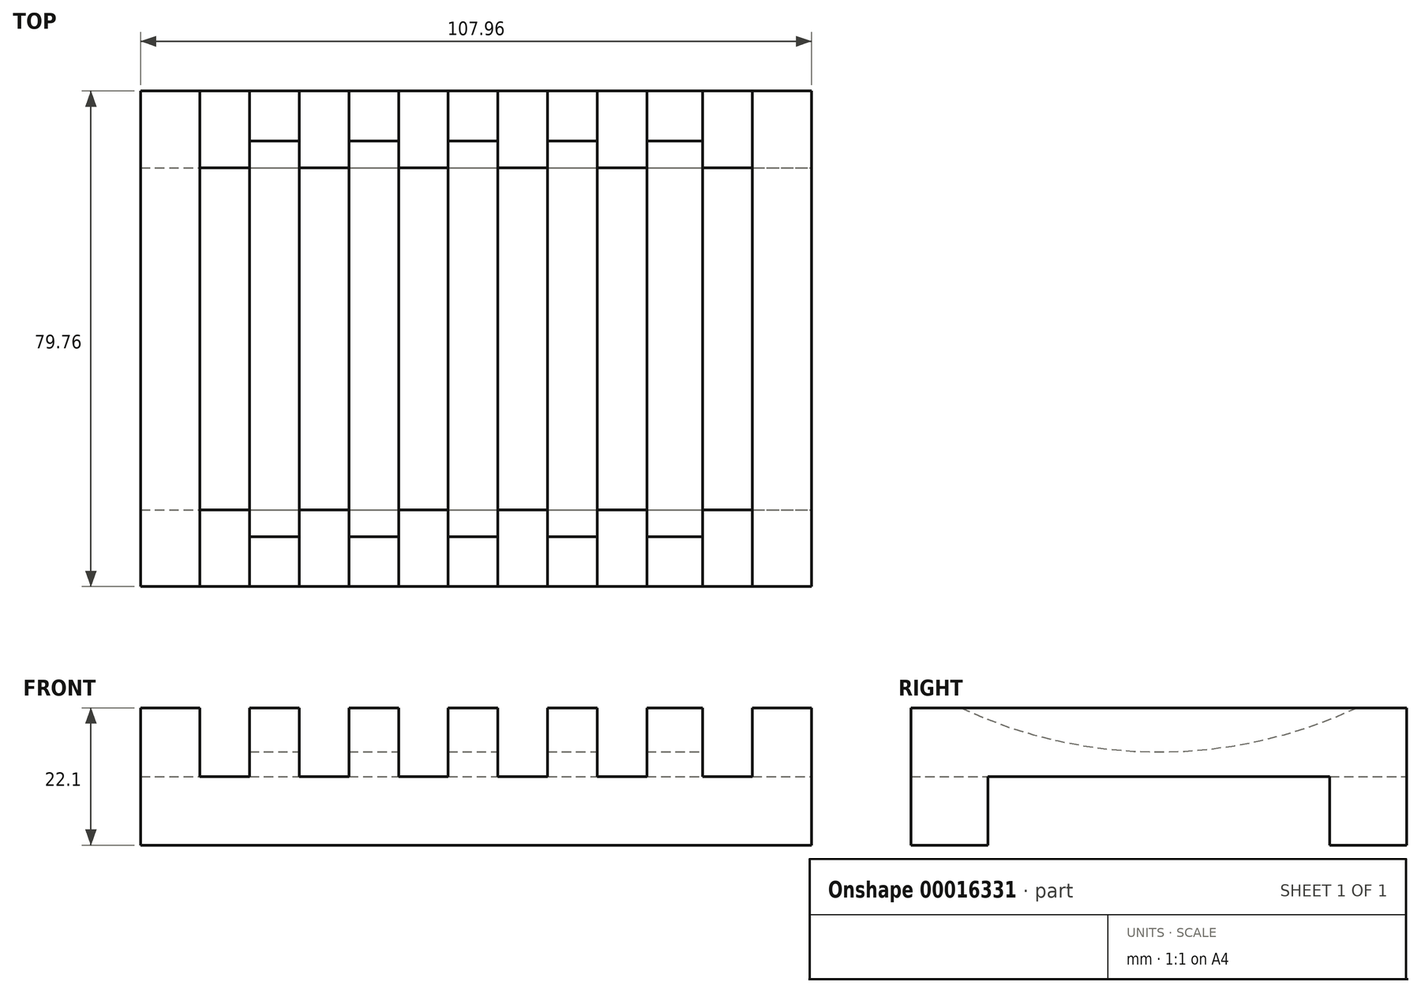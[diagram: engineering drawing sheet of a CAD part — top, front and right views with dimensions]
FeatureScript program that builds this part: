
annotation { "Feature Type Name" : "Feature", "Feature Type Description" : "" }
export const myFeature = defineFeature(function(context is Context, id is Id, definition is map)
    precondition{}
    {
        {
            var Q0;
            Q0=qCreatedBy(makeId("Top.planeOp"),FACE);
            var sketch = newSketch(context, id + "F0", { "sketchPlane" : qUnion([Q0])});
            skLineSegment(sketch, "E0.bottom", {"start": v(-53.98, 39.88) * mm, "end": v(53.97, 39.88) * mm});
            skLineSegment(sketch, "E0.top", {"start": v(-53.98, -39.88) * mm, "end": v(53.97, -39.88) * mm});
            skLineSegment(sketch, "E0.left", {"start": v(-53.98, 39.88) * mm, "end": v(-53.98, -39.88) * mm});
            skLineSegment(sketch, "E0.right", {"start": v(53.97, 39.88) * mm, "end": v(53.97, -39.88) * mm});
            skLineSegment(sketch, "E1", {"start": v(-53.98, 39.88) * mm, "end": v(53.98, -39.88) * mm, "construction": true});
            skSolve(sketch);
        }
        {
            var Q0;
            Q0 = qSketchRegion(id + "F0", true);
            extrude(context, id + "F1", {"entities" : qUnion([Q0]), "depth" : (.87 * 25.4) * mm, "offsetDistance" : 25 * mm});
        }
        {
            var Q0;
            Q0=qCreatedBy(makeId("Right.planeOp"),FACE);
            var sketch = newSketch(context, id + "F2", { "sketchPlane" : qUnion([Q0])});
            skLineSegment(sketch, "E2.bottom", {"start": v(-27.5, 11) * mm, "end": v(27.5, 11) * mm});
            skLineSegment(sketch, "E2.top", {"start": v(-27.5, 0) * mm, "end": v(27.5, 0) * mm});
            skLineSegment(sketch, "E2.left", {"start": v(-27.5, 11) * mm, "end": v(-27.5, 0) * mm});
            skLineSegment(sketch, "E2.right", {"start": v(27.5, 11) * mm, "end": v(27.5, 0) * mm});
            skSolve(sketch);
        }
        {
            var Q0;
            Q0 = qSketchRegion(id + "F2", true);
            extrude(context, id + "F3", {"entities" : qUnion([Q0]), "operationType" : NewBodyOperationType.REMOVE, "endBound" : BoundingType.SYMMETRIC, "oppositeDirection" : true, "depth" : 136.6 * mm, "offsetDistance" : 25 * mm});
        }
        {
            var Q0;
            Q0=qCreatedBy(makeId("Right.planeOp"),FACE);
            var sketch = newSketch(context, id + "F4", { "sketchPlane" : qUnion([Q0])});
            skCircle(sketch, "E3", {"center": v(0, 90) * mm, "radius": 75 * mm});
            skSolve(sketch);
        }
        {
            var Q0;
            Q0 = qSketchRegion(id + "F4", true);
            extrude(context, id + "F5", {"entities" : qUnion([Q0]), "operationType" : NewBodyOperationType.REMOVE, "endBound" : BoundingType.SYMMETRIC, "oppositeDirection" : true, "depth" : (3.5 * 25.4) * mm, "offsetDistance" : 25 * mm});
        }
        {
            var Q0;
            Q0=qCreatedBy(makeId("Front.planeOp"),FACE);
            var sketch = newSketch(context, id + "F6", { "sketchPlane" : qUnion([Q0])});
            skLineSegment(sketch, "E4.bottom", {"start": v(-44.45, 22.1) * mm, "end": v(-36.46, 22.1) * mm});
            skLineSegment(sketch, "E4.top", {"start": v(-44.45, 11) * mm, "end": v(-36.46, 11) * mm});
            skLineSegment(sketch, "E4.left", {"start": v(-44.45, 22.1) * mm, "end": v(-44.45, 11) * mm});
            skLineSegment(sketch, "E4.right", {"start": v(-36.46, 22.1) * mm, "end": v(-36.46, 11) * mm});
            skLineSegment(sketch, "E5.bottom", {"start": v(36.46, 22.1) * mm, "end": v(44.45, 22.1) * mm});
            skLineSegment(sketch, "E5.top", {"start": v(36.46, 11) * mm, "end": v(44.45, 11) * mm});
            skLineSegment(sketch, "E5.left", {"start": v(36.46, 22.1) * mm, "end": v(36.46, 11) * mm});
            skLineSegment(sketch, "E5.right", {"start": v(44.45, 22.1) * mm, "end": v(44.45, 11) * mm});
            skLineSegment(sketch, "E6.1.0.0", {"start": v(-28.47, 22.1) * mm, "end": v(-20.48, 22.1) * mm});
            skLineSegment(sketch, "E6.1.0.1", {"start": v(-28.47, 22.1) * mm, "end": v(-28.47, 11) * mm});
            skLineSegment(sketch, "E6.1.0.2", {"start": v(-20.48, 22.1) * mm, "end": v(-20.48, 11) * mm});
            skLineSegment(sketch, "E6.1.0.3", {"start": v(-28.47, 11) * mm, "end": v(-20.48, 11) * mm});
            skLineSegment(sketch, "E6.2.0.0", {"start": v(-12.49, 22.1) * mm, "end": v(-4.5, 22.1) * mm});
            skLineSegment(sketch, "E6.2.0.1", {"start": v(-12.49, 22.1) * mm, "end": v(-12.49, 11) * mm});
            skLineSegment(sketch, "E6.2.0.2", {"start": v(-4.5, 22.1) * mm, "end": v(-4.5, 11) * mm});
            skLineSegment(sketch, "E6.2.0.3", {"start": v(-12.49, 11) * mm, "end": v(-4.5, 11) * mm});
            skLineSegment(sketch, "E6.3.0.0", {"start": v(3.5, 22.1) * mm, "end": v(11.48, 22.1) * mm});
            skLineSegment(sketch, "E6.3.0.1", {"start": v(3.5, 22.1) * mm, "end": v(3.5, 11) * mm});
            skLineSegment(sketch, "E6.3.0.2", {"start": v(11.48, 22.1) * mm, "end": v(11.48, 11) * mm});
            skLineSegment(sketch, "E6.3.0.3", {"start": v(3.5, 11) * mm, "end": v(11.48, 11) * mm});
            skLineSegment(sketch, "E6.4.0.0", {"start": v(19.47, 22.1) * mm, "end": v(27.46, 22.1) * mm});
            skLineSegment(sketch, "E6.4.0.1", {"start": v(19.47, 22.1) * mm, "end": v(19.47, 11) * mm});
            skLineSegment(sketch, "E6.4.0.2", {"start": v(27.46, 22.1) * mm, "end": v(27.46, 11) * mm});
            skLineSegment(sketch, "E6.4.0.3", {"start": v(19.47, 11) * mm, "end": v(27.46, 11) * mm});
            skLineSegment(sketch, "E6.direction1", {"start": v(-44.45, 11) * mm, "end": v(-28.47, 11) * mm, "construction": true});
            skSolve(sketch);
        }
        {
            var Q0;
            Q0 = qSketchRegion(id + "F6", true);
            extrude(context, id + "F7", {"entities" : qUnion([Q0]), "operationType" : NewBodyOperationType.REMOVE, "endBound" : BoundingType.SYMMETRIC, "depth" : 95.8 * mm, "offsetDistance" : 25 * mm});
        }
    });
